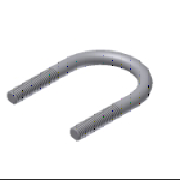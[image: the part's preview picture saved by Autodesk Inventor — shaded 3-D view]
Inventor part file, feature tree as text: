
AUTODESK INVENTOR PART (.ipt)
format: ipt  version: 2023 (Build 270158000, 158)  size: 130,560 bytes
history: native  units: mm
features: sketch x2, plane x1, sweep x1
ambient origin geometry x8: Origin, YZ Plane, XZ Plane, XY Plane, X Axis, Y Axis, Z Axis, Center Point
bodies: Solid1 (feature_tree)
feature tree (4):
  sketch  "Sketch1"  dims[d0=48.0mm d1=44.0mm]
  plane  "Work Plane1"
  sweep  "Колебание1"
  sketch  "Sketch2"  dims[d2=8.0mm d3=0.0mm d4=34.0mm d5=0.0mm d8=1.0mm d9=2.0mm d10=45.0deg d11=34.0mm d12=0.0mm d13=0.0mm]
